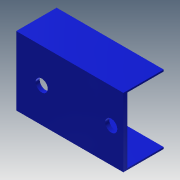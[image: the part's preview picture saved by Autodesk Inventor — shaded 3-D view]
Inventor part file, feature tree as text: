
AUTODESK INVENTOR PART (.ipt)
format: ipt  version: 2013 (Build 170138000, 138)  size: 141,824 bytes
history: native  units: mm
features: extrude x7, sketch x7
ambient origin geometry x8: Origin, YZ Plane, XZ Plane, XY Plane, X Axis, Y Axis, Z Axis, Center Point
bodies: Solid1 (feature_tree)
feature tree (14):
  extrude  "Extrusion1"  Depth=17.0mm
  extrude  "Extrusion2"  Depth=24.7mm
  extrude  "Extrusion3"  Depth=9.0mm TaperAngle=0.0deg
  extrude  "Extrusion4"  Depth=3.0mm
  extrude  "Extrusion5"  Depth=3.0mm
  extrude  "Extrusion6"  Depth=2.0mm TaperAngle=0.0deg
  extrude  "Extrusion7"  Depth=2.0mm
  sketch  "Sketch1"  dims[d0=24.7mm d1=17.0mm]
  sketch  "Sketch2"  dims[d2=10.0mm d3=0.0mm d4=24.7mm]
  sketch  "Sketch3"  dims[d5=16.2mm d6=9.0mm d7=0.0mm]
  sketch  "Sketch4"  dims[d8=3.0mm d9=3.0mm]
  sketch  "Sketch5"  dims[d10=3.0mm d11=3.0mm]
  sketch  "Sketch6"  dims[d12=1.0mm d13=0.0mm d14=2.0mm d15=0.0mm]
  sketch  "Sketch7"  dims[d16=0.2mm d17=0.0mm d18=2.0mm d19=2.0mm d20=3.0mm d21=1.0mm d22=0.0mm d29=3.3mm d30=3.0mm d31=3.0mm d32=1.0mm d33=0.0mm]
